# Revit family: 2Celite_Sobrepor_Cuba Oval_76146
name_source: partatom
category: Plumbing Fixtures
revit_build: Autodesk Revit MEP 2014 (Build: 20131024_2115(x64)
units: mm (PartAtom-declared; Revit-internal decimal feet)

## types (2) — shared parameters
Assembly Code = D2010400
Celite: Categoria = Cubas e Lavatórios
Celite: Código = 76146
Celite: Desenho Técnico = http://www.celite.com.br
Celite: Fabricante = Celite
Celite: Linha = Sobrepor
Celite: Link do Produto = http://www.celite.com.br
Celite: Norma = ABNT NBR 15097-1: 2011 - Requisitos e métodos de ensaio
Celite: Produto = Louças
Celite: Tipo = Cubas
Celite: Versão = Autodesk Revit MEP 2014
Desenvolvido por = ofcdesk
Diâmetro Ponto de Esgoto = 40 mm
Manufacturer = Celite
Model = 76146
Raio Ponto de Esgoto = 20 mm
Selo de Qualidade ofcdesk = Standard
URL = http://www.celite.com.br
WFU = 2
zero-valued in all types: CWFU, Default Elevation, HWFU

## per-type parameters (varying)
| type | Celite: Cores Disponíveis | Celite: Descrição | Description |
| Branca - 76146 | Branco | Cuba oval universal cor branca (76146), linha Sobrepor - Louças Celite | Cuba oval universal cor branca (76146), linha Sobrepor - Louças Celite |
| Pergamon - 76146 | Pergamon | Cuba oval universal cor pergamon (76146), linha Sobrepor - Louças Celite | Cuba oval universal cor pergamon (76146), linha Sobrepor - Louças Celite |

## geometry (parser evidence)
native form markers: Blend x4, Sweep x7
no freeform markers — native parametric forms only
